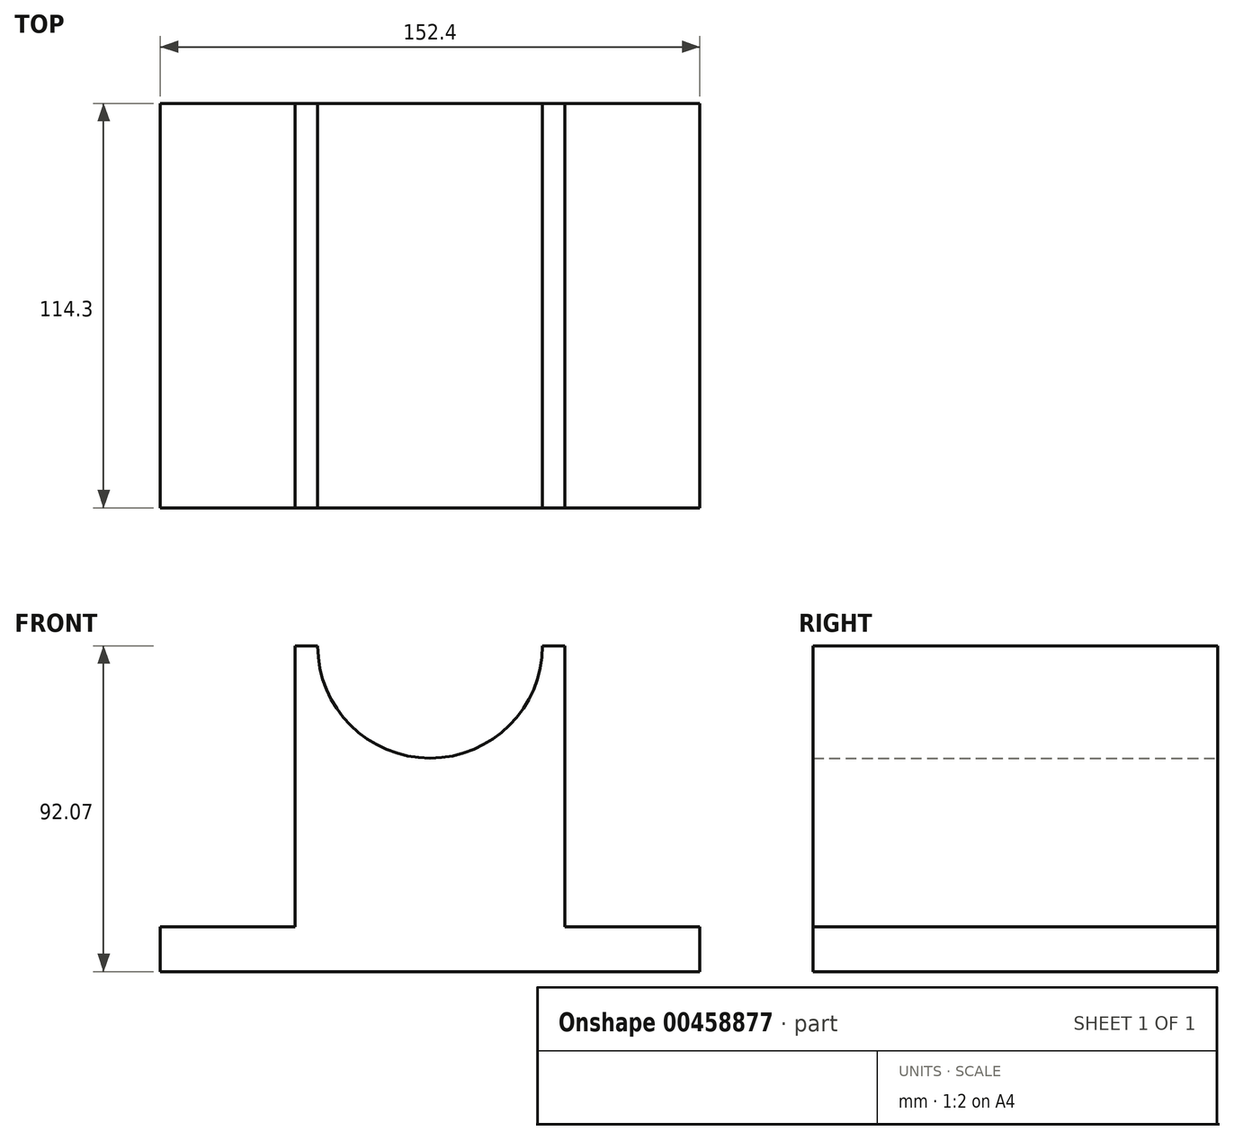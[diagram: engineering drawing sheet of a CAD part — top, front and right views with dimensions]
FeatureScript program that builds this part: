
annotation { "Feature Type Name" : "Feature", "Feature Type Description" : "" }
export const myFeature = defineFeature(function(context is Context, id is Id, definition is map)
    precondition{}
    {
        {
            var Q0;
            Q0=qCreatedBy(makeId("Front.planeOp"),FACE);
            var sketch = newSketch(context, id + "F0", { "sketchPlane" : qUnion([Q0])});
            skLineSegment(sketch, "E0", {"start": v(-76.2, -27.18) * mm, "end": v(0, -27.18) * mm});
            skLineSegment(sketch, "E1", {"start": v(-76.2, -27.18) * mm, "end": v(-76.2, -14.48) * mm});
            skLineSegment(sketch, "E2", {"start": v(-76.2, -14.48) * mm, "end": v(-38.1, -14.48) * mm});
            skLineSegment(sketch, "E3", {"start": v(-38.1, -14.48) * mm, "end": v(-38.1, 64.9) * mm});
            skLineSegment(sketch, "E4", {"start": v(-38.1, 64.9) * mm, "end": v(0, 64.9) * mm});
            skLineSegment(sketch, "E5", {"start": v(0, 64.9) * mm, "end": v(0, -27.18) * mm, "construction": true});
            skLineSegment(sketch, "E6.MirrorCS", {"start": v(38.1, 64.9) * mm, "end": v(0, 64.9) * mm});
            skLineSegment(sketch, "E7.MirrorCS", {"start": v(38.1, -14.48) * mm, "end": v(38.1, 64.9) * mm});
            skLineSegment(sketch, "E8.MirrorCS", {"start": v(76.2, -14.48) * mm, "end": v(38.1, -14.48) * mm});
            skLineSegment(sketch, "E9.MirrorCS", {"start": v(76.2, -27.18) * mm, "end": v(0, -27.18) * mm});
            skLineSegment(sketch, "E10.MirrorCS", {"start": v(76.2, -27.18) * mm, "end": v(76.2, -14.48) * mm});
            skArc(sketch, "E11", {"start": v(0, 33.14) * mm, "mid": v(22.45, 42.44) * mm, "end": v(31.75, 64.9) * mm});
            skArc(sketch, "E12.MirrorCS", {"start": v(0, 33.14) * mm, "mid": v(-22.45, 42.44) * mm, "end": v(-31.75, 64.9) * mm});
            skSolve(sketch);
        }
        {
            var Q0;
            Q0=makeQuery(id+"F0.imprint","IMPRINT",FACE,{"disambiguationData":[TD([[makeQuery(id+"F0.imprint","IMPRINT",EDGE,{"derivedFrom":sQuery(id+"F0.wireOp",EDGE,"E0")}),1.0]])]});
            extrude(context, id + "F1", {"entities" : qUnion([Q0]), "depth" : 114.3 * mm});
        }
    });
